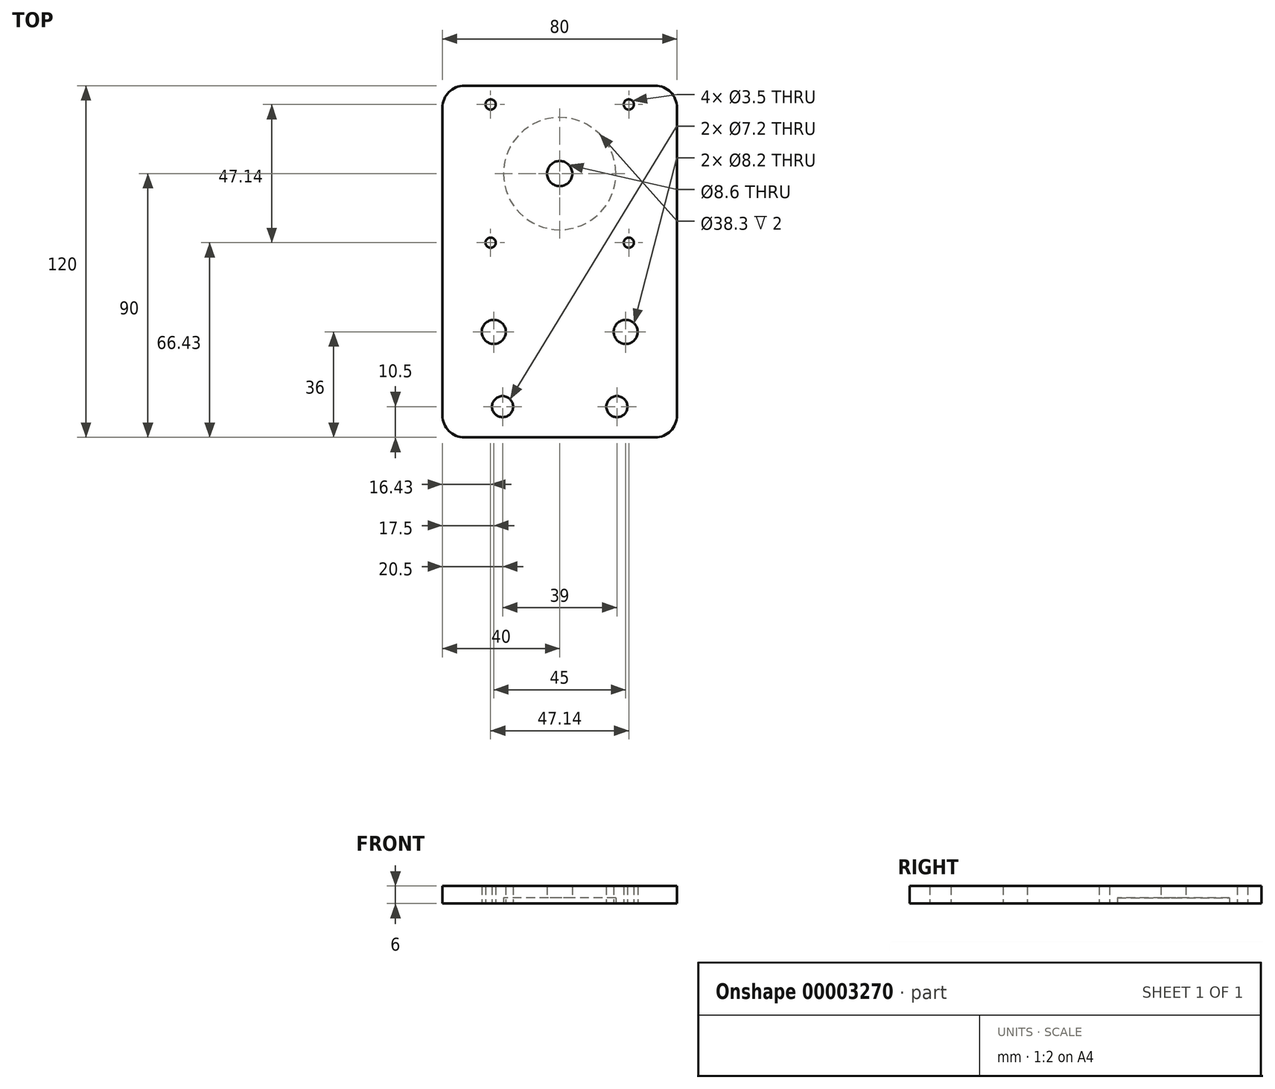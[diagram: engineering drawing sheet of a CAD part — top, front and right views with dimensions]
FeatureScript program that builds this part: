
annotation { "Feature Type Name" : "Feature", "Feature Type Description" : "" }
export const myFeature = defineFeature(function(context is Context, id is Id, definition is map)
    precondition{}
    {
        {
            var Q0;
            Q0=qCreatedBy(makeId("Top.planeOp"),FACE);
            var sketch = newSketch(context, id + "F0", { "sketchPlane" : qUnion([Q0])});
            skLineSegment(sketch, "E0.rect.bottom", {"start": v(-32.5, 60) * mm, "end": v(32.5, 60) * mm});
            skLineSegment(sketch, "E0.rect.top", {"start": v(-32.5, -60) * mm, "end": v(32.5, -60) * mm});
            skLineSegment(sketch, "E0.rect.left", {"start": v(-40, 52.5) * mm, "end": v(-40, -52.5) * mm});
            skLineSegment(sketch, "E0.rect.right", {"start": v(40, 52.5) * mm, "end": v(40, -52.5) * mm});
            skPoint(sketch, "E0.rect.middle", {"position": v(0, 0) * mm});
            skLineSegment(sketch, "E1", {"start": v(0, 0) * mm, "end": v(0, 87.7) * mm, "construction": true});
            skCircle(sketch, "E2", {"center": v(0, 30) * mm, "radius": 19.15 * mm});
            skLineSegment(sketch, "E3", {"start": v(-51.35, -49.5) * mm, "end": v(61.53, -49.5) * mm, "construction": true});
            skCircle(sketch, "E4", {"center": v(-23.57, 53.57) * mm, "radius": 1.75 * mm});
            skCircle(sketch, "E5", {"center": v(-23.57, 6.43) * mm, "radius": 1.75 * mm});
            skCircle(sketch, "E6", {"center": v(23.57, 6.43) * mm, "radius": 1.75 * mm});
            skCircle(sketch, "E7", {"center": v(23.57, 53.57) * mm, "radius": 1.75 * mm});
            skCircle(sketch, "E8", {"center": v(-19.5, -49.5) * mm, "radius": 3.6 * mm});
            skCircle(sketch, "E9", {"center": v(19.5, -49.5) * mm, "radius": 3.6 * mm});
            skCircle(sketch, "E10", {"center": v(-22.5, -24) * mm, "radius": 4.1 * mm});
            skCircle(sketch, "E11", {"center": v(22.5, -24) * mm, "radius": 4.1 * mm});
            skLineSegment(sketch, "E12", {"start": v(-46.68, 30) * mm, "end": v(46.68, 30) * mm, "construction": true});
            skLineSegment(sketch, "E13", {"start": v(-47, -24) * mm, "end": v(46.05, -24) * mm, "construction": true});
            skPoint(sketch, "E14.visualSharp", {"position": v(40, 60) * mm});
            skArc(sketch, "E14.filletArc", {"start": v(40, 52.5) * mm, "mid": v(37.8, 57.8) * mm, "end": v(32.5, 60) * mm});
            skPoint(sketch, "E15.visualSharp", {"position": v(-40, 60) * mm});
            skArc(sketch, "E15.filletArc", {"start": v(-32.5, 60) * mm, "mid": v(-37.8, 57.8) * mm, "end": v(-40, 52.5) * mm});
            skPoint(sketch, "E16.visualSharp", {"position": v(40, -60) * mm});
            skArc(sketch, "E16.filletArc", {"start": v(32.5, -60) * mm, "mid": v(37.8, -57.8) * mm, "end": v(40, -52.5) * mm});
            skPoint(sketch, "E17.visualSharp", {"position": v(-40, -60) * mm});
            skArc(sketch, "E17.filletArc", {"start": v(-40, -52.5) * mm, "mid": v(-37.8, -57.8) * mm, "end": v(-32.5, -60) * mm});
            skCircle(sketch, "E18", {"center": v(-19.5, -49.5) * mm, "radius": 16 * mm, "construction": true});
            skCircle(sketch, "E19", {"center": v(19.5, -49.5) * mm, "radius": 16 * mm, "construction": true});
            skLineSegment(sketch, "E20", {"start": v(-18.99, -65.5) * mm, "end": v(44.24, -65.5) * mm, "construction": true});
            skCircle(sketch, "E21", {"center": v(0, 30) * mm, "radius": 4.3 * mm});
            skSolve(sketch);
        }
        {
            var Q0;
            Q0=makeQuery(id+"F0.imprint","IMPRINT",FACE,{"disambiguationData":[TD([[makeQuery(id+"F0.imprint","IMPRINT",EDGE,{"derivedFrom":sQuery(id+"F0.wireOp",EDGE,"E0.rect.bottom")}),-1.0]])]});
            var Q1;
            Q1=makeQuery(id+"F0.imprint","IMPRINT",FACE,{"disambiguationData":[TD([[makeQuery(id+"F0.imprint","IMPRINT",EDGE,{"derivedFrom":sQuery(id+"F0.wireOp",EDGE,"E2")}),1.0]])]});
            extrude(context, id + "F1", {"entities" : qUnion([Q0, Q1]), "depth" : 6 * mm});
        }
        {
            var Q0;
            Q0=makeQuery(id+"F0.imprint","IMPRINT",FACE,{"disambiguationData":[TD([[makeQuery(id+"F0.imprint","IMPRINT",EDGE,{"derivedFrom":sQuery(id+"F0.wireOp",EDGE,"E2")}),1.0]])]});
            extrude(context, id + "F2", {"entities" : qUnion([Q0]), "operationType" : NewBodyOperationType.REMOVE, "depth" : 2 * mm});
        }
    });
